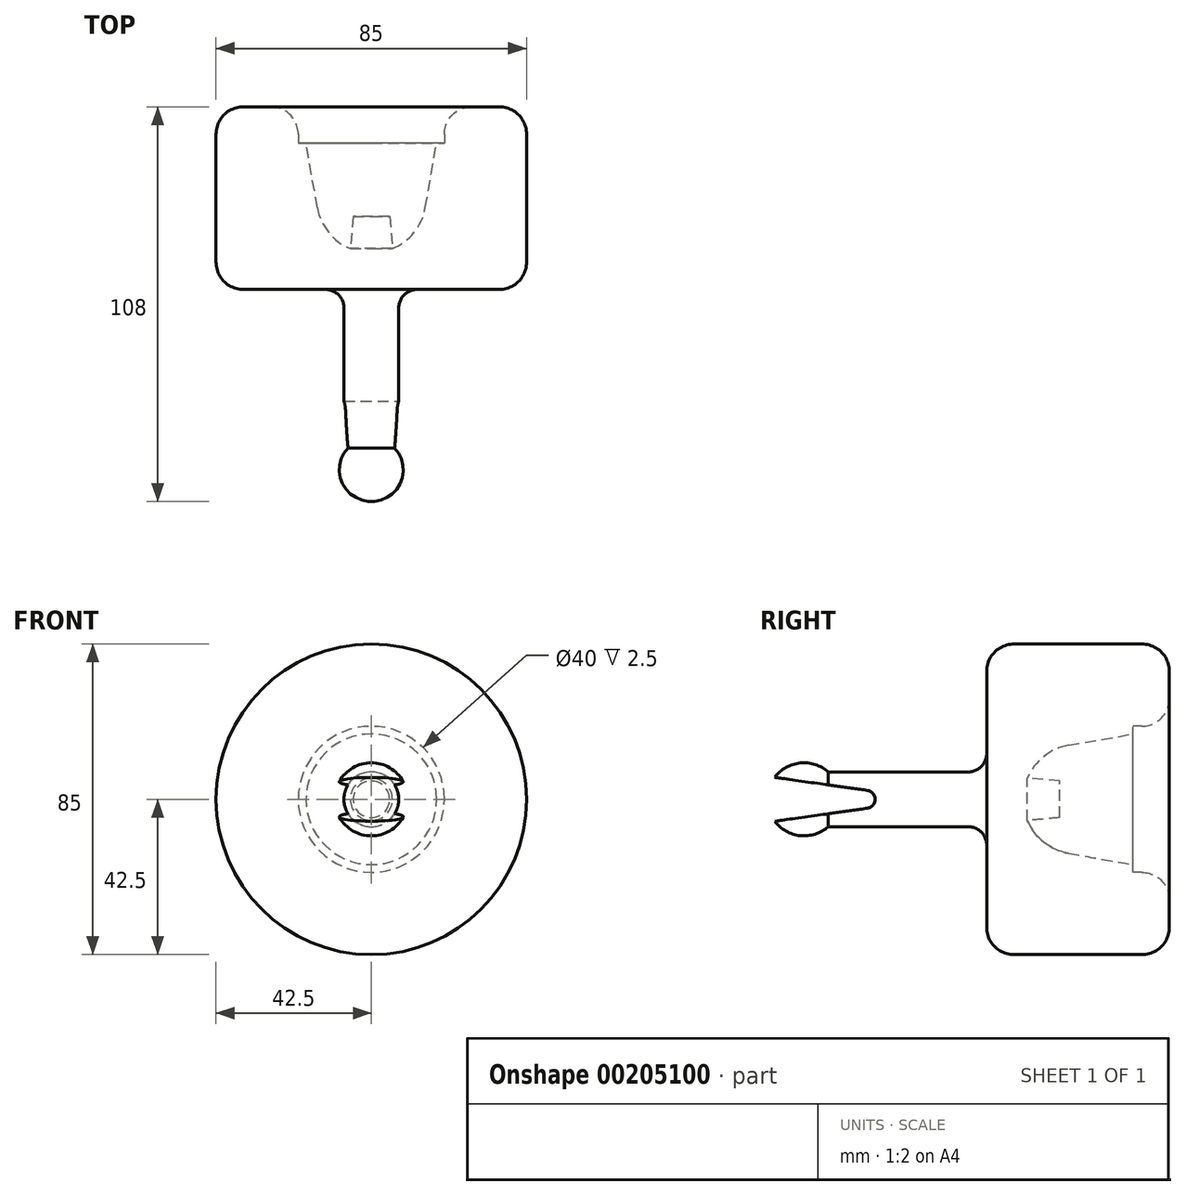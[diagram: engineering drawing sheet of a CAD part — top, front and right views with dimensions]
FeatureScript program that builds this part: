
annotation { "Feature Type Name" : "Feature", "Feature Type Description" : "" }
export const myFeature = defineFeature(function(context is Context, id is Id, definition is map)
    precondition{}
    {
        {
            var Q0;
            Q0=qCreatedBy(makeId("Right.planeOp"),FACE);
            var sketch = newSketch(context, id + "F0", { "sketchPlane" : qUnion([Q0])});
            skArc(sketch, "E0", {"start": v(6.61, 7.5) * mm, "mid": v(-4.11, 9.11) * mm, "end": v(-10, 0) * mm});
            skLineSegment(sketch, "E1", {"start": v(-10, 0) * mm, "end": v(70, 0) * mm});
            skLineSegment(sketch, "E2", {"start": v(6.61, 7.5) * mm, "end": v(45, 7.5) * mm});
            skLineSegment(sketch, "E3", {"start": v(50, 12.5) * mm, "end": v(50, 35) * mm});
            skLineSegment(sketch, "E4", {"start": v(57.5, 42.5) * mm, "end": v(92.5, 42.5) * mm});
            skLineSegment(sketch, "E5", {"start": v(100, 35) * mm, "end": v(100, 27.5) * mm});
            skLineSegment(sketch, "E6", {"start": v(92.5, 20) * mm, "end": v(90, 20) * mm});
            skLineSegment(sketch, "E7", {"start": v(90, 20) * mm, "end": v(90, 17.88) * mm});
            skLineSegment(sketch, "E8", {"start": v(61.16, 5.77) * mm, "end": v(70, 5) * mm});
            skLineSegment(sketch, "E9", {"start": v(70, 5) * mm, "end": v(70, 0) * mm});
            skLineSegment(sketch, "E10", {"start": v(90, 17.88) * mm, "end": v(72.4, 14.77) * mm});
            skArc(sketch, "E11", {"start": v(72.4, 14.77) * mm, "mid": v(65.63, 11.7) * mm, "end": v(61.16, 5.77) * mm});
            skPoint(sketch, "E12.visualSharp", {"position": v(50, 42.5) * mm});
            skArc(sketch, "E12.filletArc", {"start": v(57.5, 42.5) * mm, "mid": v(52.2, 40.3) * mm, "end": v(50, 35) * mm});
            skPoint(sketch, "E13.visualSharp", {"position": v(100, 42.5) * mm});
            skArc(sketch, "E13.filletArc", {"start": v(100, 35) * mm, "mid": v(97.8, 40.3) * mm, "end": v(92.5, 42.5) * mm});
            skPoint(sketch, "E14.visualSharp", {"position": v(50, 7.5) * mm});
            skArc(sketch, "E14.filletArc", {"start": v(45, 7.5) * mm, "mid": v(48.54, 8.96) * mm, "end": v(50, 12.5) * mm});
            skPoint(sketch, "E15.visualSharp", {"position": v(100, 20) * mm});
            skArc(sketch, "E15.filletArc", {"start": v(92.5, 20) * mm, "mid": v(97.8, 22.2) * mm, "end": v(100, 27.5) * mm});
            skSolve(sketch);
        }
        {
            var Q0;
            Q0=makeQuery(id+"F0.imprint","IMPRINT",FACE,{"disambiguationData":[TD([[makeQuery(id+"F0.imprint","IMPRINT",EDGE,{"derivedFrom":sQuery(id+"F0.wireOp",EDGE,"E0")}),1.0]])]});
            var Q1;
            Q1 = qConstructionFilter(qBodyType(qCreatedBy(id + "F0" ,EDGE), BodyType.WIRE), ConstructionObject.NO);
            var Q2;
            Q2=sQuery(id+"F0.wireOp",EDGE,"E1");
            revolve(context, id + "F1", {"entities" : qUnion([Q0]), "surfaceEntities" : qUnion([Q1]), "axis" : qUnion([Q2]), "revolveType" : RevolveType.FULL});
        }
        {
            var Q0;
            Q0=qCreatedBy(makeId("Right.planeOp"),FACE);
            var sketch = newSketch(context, id + "F2", { "sketchPlane" : qUnion([Q0])});
            skLineSegment(sketch, "E16", {"start": v(-10, 0) * mm, "end": v(100, 0) * mm, "construction": true});
            skLineSegment(sketch, "E17", {"start": v(-8, 6) * mm, "end": v(17.34, 2.44) * mm});
            skArc(sketch, "E18", {"start": v(17.34, 2.44) * mm, "mid": v(18.86, 1.62) * mm, "end": v(19.46, 0) * mm});
            skLineSegment(sketch, "E19.MirrorCS", {"start": v(-8, -6) * mm, "end": v(17.34, -2.44) * mm});
            skArc(sketch, "E20.MirrorCS", {"start": v(17.34, -2.44) * mm, "mid": v(18.86, -1.62) * mm, "end": v(19.46, 0) * mm});
            skArc(sketch, "E21", {"start": v(-8, 6) * mm, "mid": v(-10, 0) * mm, "end": v(-8, -6) * mm});
            skSolve(sketch);
        }
        {
            var Q0;
            Q0 = qSketchRegion(id + "F2", true);
            extrude(context, id + "F3", {"entities" : qUnion([Q0]), "operationType" : NewBodyOperationType.REMOVE, "endBound" : BoundingType.THROUGH_ALL, "oppositeDirection" : true, "depth" : 25 * mm, "hasSecondDirection" : true, "secondDirectionBound" : SecondDirectionBoundingType.THROUGH_ALL, "secondDirectionOppositeDirection" : false, "secondDirectionDepth" : 25 * mm});
        }
    });
